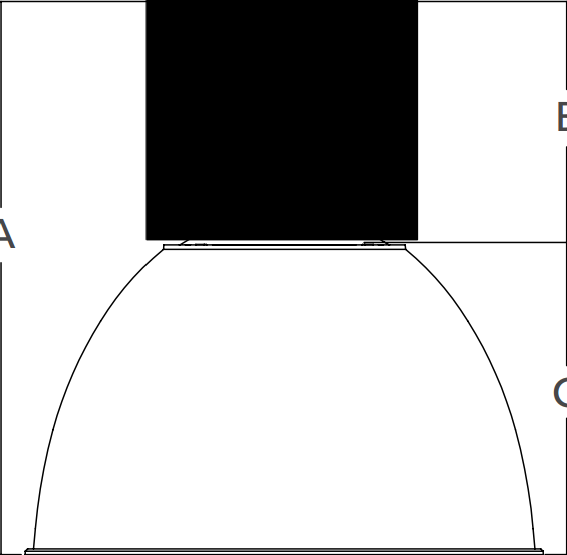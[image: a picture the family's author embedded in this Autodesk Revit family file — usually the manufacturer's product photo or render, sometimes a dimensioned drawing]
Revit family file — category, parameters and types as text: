
# Revit family: SAV
name_source: partatom
category: Lighting Fixtures
units: mm (PartAtom-declared; Revit-internal decimal feet)

## family parameters
Cut with Voids When Loaded = No
Host = Face
Light Source = No
OmniClass Number = 23.80.70.11.11
OmniClass Title = General Luminaries, Non Directional
Part Type = Normal
Room Calculation Point = No
Round Connector Dimension = Use Diameter
Shared = No

## types (8) — shared parameters
Apparent Load = 73 VA
Default Elevation = 48.000"
Description = The Savvano™ is a decorative highbay available in a wide range of decorator friendly colors.
Glass Lens = White Glass
Lamp = LED Highbay
Load Classification = Lighting
Manufacturer = Columbia Lighting
Model = Savvano-Decorative LED High Bay
Power Factor = 1
URL = https://www.currentlighting.com
Voltage = 120 V
Wattage = 73 W
Wattage Comments = Total input wattage of 73W/95W/153W/177W/219W

## per-type parameters (varying)
| type | Finish | Is 16 | Is 22 | Photometrics |
| SAV-RD | Red | No | Yes | Web SAV : SAV-ML-40-8-WW22-CLR-U-GG |
| SAV-WW | White | Yes | No | Web SAV : SAV-ML-40-8-WW22-CLR-U-GG |
| SAV-GG | Gray | Yes | No | Web SAV : SAV-ML-40-8-WW22-CLR-U-GG |
| SAV-BL | Black | No | Yes | Web SAV : SAV-LX-27-8-SB16-P95-U-GG |
| SAV-BS | Blue | Yes | No | Web SAV : SAV-ML-40-8-WW22-CLR-U-GG |
| SAV-CH | Champagne | Yes | No | Web SAV : SAV-ML-40-8-WW22-CLR-U-GG |
| SAV-SB | Serenity Blue | No | Yes | Web SAV : SAV-ML-40-8-WW22-CLR-U-GG |
| SAV-WN | Wine | No | Yes | Web SAV : SAV-ML-40-8-WW22-CLR-U-GG |

## geometry (parser evidence)
native form markers: Blend x33, Sweep x11
no freeform markers — native parametric forms only
